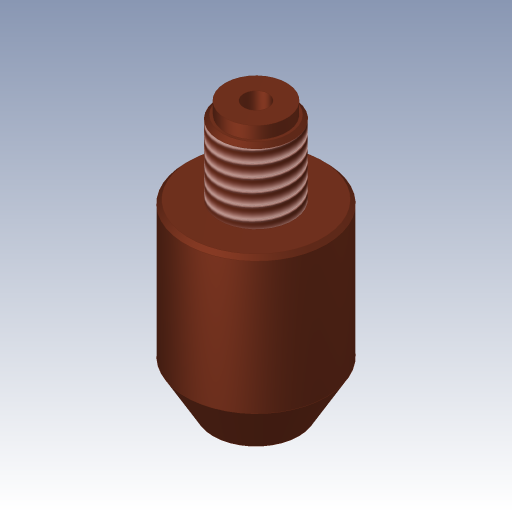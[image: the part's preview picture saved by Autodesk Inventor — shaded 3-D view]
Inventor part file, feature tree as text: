
AUTODESK INVENTOR PART (.ipt)
format: ipt  version: 2023.3 (Build 273359000, 359)  size: 204,288 bytes
history: native  units: in
note: dims shown in document units (in); Inventor stores cm internally (conversion verified against a paired STEP export)
features: sketch x2, revolve x1, thread x1, chamfer x1, hole x1
ambient origin geometry x8: Origin, YZ Plane, XZ Plane, XY Plane, X Axis, Y Axis, Z Axis, Center Point
bodies: Body1 (feature_tree)
feature tree (6):
  revolve  "Umdrehung1"
  thread  "Gewinde1"  [1 undecoded]
  chamfer  "Fase1"  Distance=0.2362in
  hole  "Bohrung1"  [1 undecoded]
  sketch  "Skizze3"  dims[d8=0.5906in]
  sketch  "Skizze4"  dims[d9=0.4528in d10=0.2362in d11=0.2362in d12=0.1969in d13=0.0394in d14=120.0deg d15=0.0787in d16=90.0deg d17=0.5906in d18=0.0in d19=0.0118in d20=0.0787in d21=45.0deg d22=0.1936in d23=0.1969in d24=0.1575in d25=0.0787in d26=90.0deg d27=0.1969in d28=0.0in]
note: 2 required parameter values undecoded (feature->parameter linkage not recoverable at this tier; creation-order binding heuristic only, values carry confidence <= 0.55)
